# Revit family: Halter Doppel-C-Profil 45- 90, VA
name_source: partatom
category: HLS-Bauteile
revit_build: Autodesk Revit 2017 (Build: 20190507_1515(x64)
units: mm (PartAtom-declared; Revit-internal decimal feet)

## family parameters
Basisbauteil = Fläche
Beim Laden mit Abzugskörper schneiden = Nein
Bemaßung runder Anschluss = Durchmesser verwenden
Gemeinsam genutzt = Ja
Raumberechnungspunkt = Nein
Teiletyp = Normal

## types (2) — shared parameters
Ausrichtung Platte = längs
Befestigung = Baukörper
Breite Platte = 70 mm  [stored 0.229659 ft]
Fabrikat = MEFA
Gewicht = 1.27 kg
Gewicht pro Bauteil = 1.27 kg
Kurztext2 = für Doppel-C-Profil 45/90
Langloch = 13x20 mm
Lochabstand = 144 mm
Lochdurchmesser = 13 mm
Länge Platte = 186 mm  [stored 0.610236 ft]
Material = Edelstahl
Profil = Doppel-C-Profil
Profilname = 45/90
Profiltyp = 45/90
Stärke Platte = 8 mm  [stored 0.0262467 ft]
Vorgabe-Ansicht = 1219 mm
max. Profilhöhe = 90 mm  [stored 0.295276 ft]
max. zul. Last Druck = 0.00 kip
zero-valued in all types: Länge, Sicherheitsfaktor

## per-type parameters (varying)
| type | Artikelnummer | EAN | Kurztext1 |
| Halter Doppel C-Profil 45- 90, V2A | 048020901 | 4250928457363 | Halter Doppel-C-Profil 45 längs V2A |
| Halter Doppel C-Profil 45- 90, V4A | 048120901 | 4250928457370 | Halter Doppel-C-Profil 45 längs V4A |

note: [stored X ft] marks values corroborated as IEEE doubles in the binary element streams (Revit-internal decimal feet)
